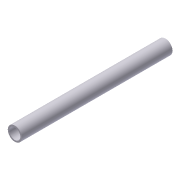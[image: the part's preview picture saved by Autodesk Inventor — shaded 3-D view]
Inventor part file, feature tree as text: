
AUTODESK INVENTOR PART (.ipt)
format: ipt  version: unknown  size: 152,576 bytes
history: native  units: in
note: dims shown in document units (in); Inventor stores cm internally (conversion verified against a paired STEP export)
features: extrude x1, sketch x1
ambient origin geometry x8: Origin, YZ Plane, XZ Plane, XY Plane, X Axis, Y Axis, Z Axis, Center Point
feature tree (2):
  extrude  "Extrusion1"  Depth=1.3125in
  sketch  "Sketch1"  dims[d0=1.0313in d1=1.3125in d2=14.0in d3=0.0in]
